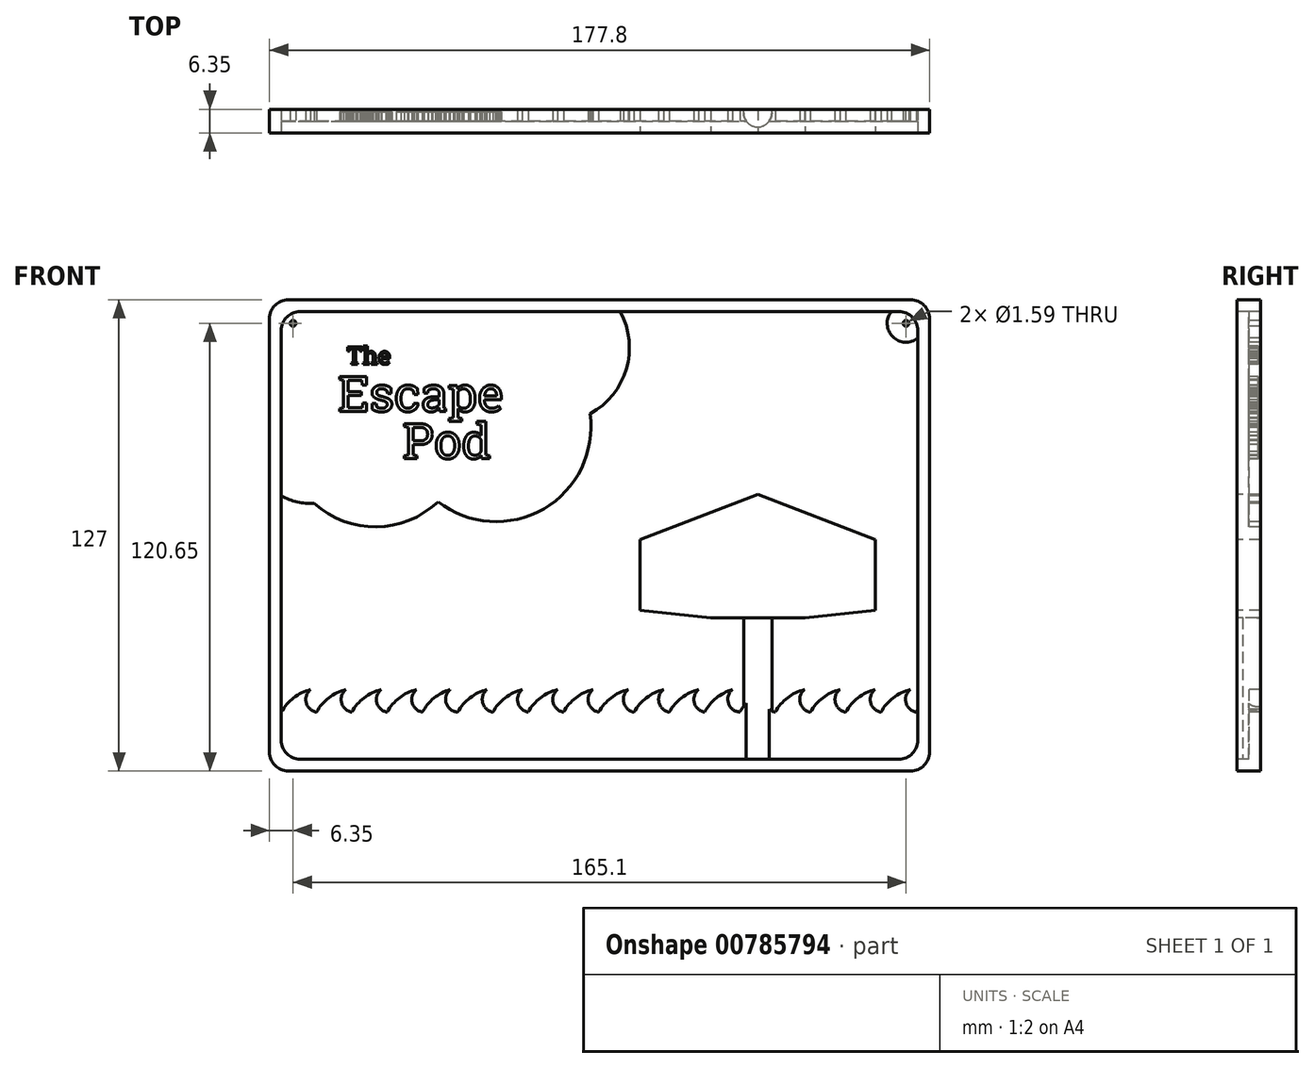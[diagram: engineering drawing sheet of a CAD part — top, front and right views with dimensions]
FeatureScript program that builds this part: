
annotation { "Feature Type Name" : "Feature", "Feature Type Description" : "" }
export const myFeature = defineFeature(function(context is Context, id is Id, definition is map)
    precondition{}
    {
        {
            var Q0;
            Q0=qCreatedBy(makeId("Front.planeOp"),FACE);
            var sketch = newSketch(context, id + "F0", { "sketchPlane" : qUnion([Q0])});
            skLineSegment(sketch, "E0.bottom", {"start": v(0, 0) * mm, "end": v(177.8, 0) * mm});
            skLineSegment(sketch, "E0.top", {"start": v(0, 127) * mm, "end": v(177.8, 127) * mm});
            skLineSegment(sketch, "E0.left", {"start": v(0, 0) * mm, "end": v(0, 127) * mm});
            skLineSegment(sketch, "E0.right", {"start": v(177.8, 0) * mm, "end": v(177.8, 127) * mm});
            skSolve(sketch);
        }
        {
            var Q0;
            Q0 = qSketchRegion(id + "F0", true);
            extrude(context, id + "F1", {"entities" : qUnion([Q0]), "depth" : 6.35 * mm, "offsetDistance" : 25.4 * mm});
        }
        {
            var Q0;
            Q0=makeQuery(id+"F1.opExtrude","CAP_FACE",FACE,{"disambiguationData":[OSD([sQuery(id+"F0.wireOp",EDGE,"E0.bottom"),sQuery(id+"F0.wireOp",EDGE,"E0.top"),sQuery(id+"F0.wireOp",EDGE,"E0.left"),sQuery(id+"F0.wireOp",EDGE,"E0.right")])],"isStart":false});
            var sketch = newSketch(context, id + "F2", { "sketchPlane" : qUnion([Q0])});
            skLineSegment(sketch, "E1.bottom", {"start": v(3.17, 123.83) * mm, "end": v(174.62, 123.83) * mm});
            skLineSegment(sketch, "E1.top", {"start": v(3.18, 3.17) * mm, "end": v(174.62, 3.17) * mm});
            skLineSegment(sketch, "E1.left", {"start": v(3.17, 123.83) * mm, "end": v(3.18, 3.17) * mm});
            skLineSegment(sketch, "E1.right", {"start": v(174.62, 123.83) * mm, "end": v(174.62, 3.18) * mm});
            skSolve(sketch);
        }
        {
            var Q0;
            Q0=makeQuery(id+"F2.imprint","IMPRINT",FACE,{"disambiguationData":[TD([[makeQuery(id+"F2.imprint","IMPRINT",EDGE,{"derivedFrom":sQuery(id+"F2.wireOp",EDGE,"E1.bottom")}),-1.0]])]});
            extrude(context, id + "F3", {"entities" : qUnion([Q0]), "operationType" : NewBodyOperationType.REMOVE, "oppositeDirection" : true, "depth" : 3.17 * mm, "offsetDistance" : 25.4 * mm});
        }
        {
            var Q0;
            Q0=makeQuery(id+"F1.opExtrude","SWEPT_EDGE",EDGE,{"disambiguationData":[OSD([sQuery(id+"F0.wireOp",EDGE,"E0.top"),sQuery(id+"F0.wireOp",EDGE,"E0.left")])]});
            var Q1;
            Q1=makeQuery(id+"F3.boolean.opBoolean","COPY",EDGE,{"derivedFrom":makeQuery(id+"F3.opExtrude","SWEPT_EDGE",EDGE,{"disambiguationData":[OSD([sQuery(id+"F2.wireOp",EDGE,"E1.bottom"),sQuery(id+"F2.wireOp",EDGE,"E1.left")])]})});
            var Q2;
            Q2=makeQuery(id+"F1.opExtrude","SWEPT_EDGE",EDGE,{"disambiguationData":[OSD([sQuery(id+"F0.wireOp",EDGE,"E0.top"),sQuery(id+"F0.wireOp",EDGE,"E0.right")])]});
            var Q3;
            Q3=makeQuery(id+"F3.boolean.opBoolean","COPY",EDGE,{"derivedFrom":makeQuery(id+"F3.opExtrude","SWEPT_EDGE",EDGE,{"disambiguationData":[OSD([sQuery(id+"F2.wireOp",EDGE,"E1.bottom"),sQuery(id+"F2.wireOp",EDGE,"E1.right")])]})});
            var Q4;
            Q4=makeQuery(id+"F1.opExtrude","SWEPT_EDGE",EDGE,{"disambiguationData":[OSD([sQuery(id+"F0.wireOp",EDGE,"E0.bottom"),sQuery(id+"F0.wireOp",EDGE,"E0.right")])]});
            var Q5;
            Q5=makeQuery(id+"F3.boolean.opBoolean","COPY",EDGE,{"derivedFrom":makeQuery(id+"F3.opExtrude","SWEPT_EDGE",EDGE,{"disambiguationData":[OSD([sQuery(id+"F2.wireOp",EDGE,"E1.top"),sQuery(id+"F2.wireOp",EDGE,"E1.right")])]})});
            var Q6;
            Q6=makeQuery(id+"F1.opExtrude","SWEPT_EDGE",EDGE,{"disambiguationData":[OSD([sQuery(id+"F0.wireOp",EDGE,"E0.bottom"),sQuery(id+"F0.wireOp",EDGE,"E0.left")])]});
            var Q7;
            Q7=makeQuery(id+"F3.boolean.opBoolean","COPY",EDGE,{"derivedFrom":makeQuery(id+"F3.opExtrude","SWEPT_EDGE",EDGE,{"disambiguationData":[OSD([sQuery(id+"F2.wireOp",EDGE,"E1.top"),sQuery(id+"F2.wireOp",EDGE,"E1.left")])]})});
            fillet(context, id + "F4", {"entities" : qUnion([Q0, Q1, Q2, Q3, Q4, Q5, Q6, Q7]), "radius" : 5.08 * mm, "tangentPropagation" : true, "allowEdgeOverflow" : false});
        }
        {
            var Q0;
            Q0=makeQuery(id+"F3.boolean.opBoolean","COPY",FACE,{"derivedFrom":makeQuery(id+"F3.opExtrude","CAP_FACE",FACE,{"disambiguationData":[OSD([sQuery(id+"F2.wireOp",EDGE,"E1.bottom"),sQuery(id+"F2.wireOp",EDGE,"E1.top"),sQuery(id+"F2.wireOp",EDGE,"E1.left"),sQuery(id+"F2.wireOp",EDGE,"E1.right")])],"isStart":false})});
            var sketch = newSketch(context, id + "F5", { "sketchPlane" : qUnion([Q0])});
            skArc(sketch, "E2", {"start": v(3.17, 74.14) * mm, "mid": v(7.49, 72.53) * mm, "end": v(12.07, 72.13) * mm});
            skLineSegment(sketch, "E3", {"start": v(47.44, 123.83) * mm, "end": v(148.94, 123.83) * mm});
            skLineSegment(sketch, "E4", {"start": v(3.17, 74.14) * mm, "end": v(3.17, 123.83) * mm});
            skLineSegment(sketch, "E5", {"start": v(47.44, 123.83) * mm, "end": v(3.17, 123.83) * mm});
            skArc(sketch, "E6", {"start": v(86.34, 96.26) * mm, "mid": v(96.1, 108.36) * mm, "end": v(94.49, 123.83) * mm});
            skArc(sketch, "E7", {"start": v(45.38, 72.57) * mm, "mid": v(73.83, 70.63) * mm, "end": v(86.34, 96.26) * mm});
            skArc(sketch, "E8", {"start": v(12.07, 72.13) * mm, "mid": v(28.81, 65.8) * mm, "end": v(45.38, 72.57) * mm});
            skSolve(sketch);
        }
        {
            var Q0;
            {var subQ0=sQuery(id+"F5.wireOp",EDGE,"E2");Q0=makeQuery(id+"F5.imprint","IMPRINT",FACE,{"disambiguationData":[TD([[makeQuery(id+"F5.imprint","IMPRINT",EDGE,{"derivedFrom":subQ0}),1.0]])]});}
            var sketch = newSketch(context, id + "F6", { "sketchPlane" : qUnion([Q0])});
            skText(sketch, "E9", { "text": "The", "fontName": "RobotoSlab-Regular.ttf"});
            skText(sketch, "E10", { "text": "Escape", "fontName": "RobotoSlab-Regular.ttf"});
            skText(sketch, "E11", { "text": "Pod", "fontName": "RobotoSlab-Regular.ttf"});
            const initialGuessF6  = {"E9": [0.02091, 0.1096, 1, 0, 0.0047], "E10": [0.01841, 0.0969, 1, 0, 0.00952], "E11": [0.03591, 0.0842, 1, 0, 0.00952]};
            skSetInitialGuess(sketch, initialGuessF6);
            skSolve(sketch);
        }
        {
            var Q0;
            Q0 = qSketchRegion(id + "F6", true);
            extrude(context, id + "F7", {"entities" : qUnion([Q0]), "operationType" : NewBodyOperationType.REMOVE, "oppositeDirection" : true, "depth" : 2.54 * mm, "offsetDistance" : 25.4 * mm});
        }
        {
            var Q0;
            {var subQ10=sQuery(id+"F5.wireOp",EDGE,"E2");Q0=makeQuery(id+"F5.imprint","IMPRINT",FACE,{"disambiguationData":[TD([[makeQuery(id+"F5.imprint","IMPRINT",EDGE,{"derivedFrom":subQ10}),-1.0]])]});}
            var sketch = newSketch(context, id + "F8", { "sketchPlane" : qUnion([Q0])});
            skSolve(sketch);
        }
        {
            var Q0;
            {var subQ10=sQuery(id+"F5.wireOp",EDGE,"E2");Q0=makeQuery(id+"F8.imprint","IMPRINT",FACE,{"disambiguationData":[TD([[makeQuery(id+"F8.imprint","IMPRINT",EDGE,{"derivedFrom":makeQuery(id+"F5.imprint","IMPRINT",EDGE,{"derivedFrom":subQ10})}),-1.0]])]});}
            var sketch = newSketch(context, id + "F9", { "sketchPlane" : qUnion([Q0])});
            skLineSegment(sketch, "E12.top", {"start": v(3.17, 3.17) * mm, "end": v(174.62, 3.17) * mm});
            skLineSegment(sketch, "E12.left", {"start": v(3.17, 28.58) * mm, "end": v(3.18, 3.17) * mm});
            skLineSegment(sketch, "E12.right", {"start": v(174.62, 66.14) * mm, "end": v(174.62, 3.17) * mm});
            skArc(sketch, "E13", {"start": v(11.09, 21.94) * mm, "mid": v(6.51, 19.72) * mm, "end": v(3.17, 15.88) * mm});
            skArc(sketch, "E14", {"start": v(11.09, 21.94) * mm, "mid": v(9.91, 18.4) * mm, "end": v(12.68, 15.88) * mm});
            skArc(sketch, "E15", {"start": v(20.59, 21.94) * mm, "mid": v(16.01, 19.72) * mm, "end": v(12.68, 15.88) * mm});
            skArc(sketch, "E16", {"start": v(20.59, 21.94) * mm, "mid": v(19.41, 18.4) * mm, "end": v(22.18, 15.88) * mm});
            skArc(sketch, "E17", {"start": v(30.09, 21.94) * mm, "mid": v(25.51, 19.72) * mm, "end": v(22.18, 15.88) * mm});
            skArc(sketch, "E18", {"start": v(30.09, 21.94) * mm, "mid": v(28.91, 18.4) * mm, "end": v(31.68, 15.88) * mm});
            skArc(sketch, "E19", {"start": v(39.59, 21.94) * mm, "mid": v(35.01, 19.72) * mm, "end": v(31.68, 15.88) * mm});
            skArc(sketch, "E20", {"start": v(39.59, 21.94) * mm, "mid": v(38.41, 18.4) * mm, "end": v(41.18, 15.88) * mm});
            skArc(sketch, "E21", {"start": v(48.67, 21.94) * mm, "mid": v(44.33, 19.65) * mm, "end": v(41.18, 15.88) * mm});
            skArc(sketch, "E22", {"start": v(48.67, 21.94) * mm, "mid": v(47.6, 18.22) * mm, "end": v(50.68, 15.88) * mm});
            skArc(sketch, "E23", {"start": v(58.59, 21.94) * mm, "mid": v(54.01, 19.72) * mm, "end": v(50.68, 15.88) * mm});
            skArc(sketch, "E24", {"start": v(58.59, 21.94) * mm, "mid": v(57.41, 18.4) * mm, "end": v(60.18, 15.88) * mm});
            skArc(sketch, "E25", {"start": v(68.09, 21.94) * mm, "mid": v(63.51, 19.72) * mm, "end": v(60.18, 15.88) * mm});
            skArc(sketch, "E26", {"start": v(68.09, 21.94) * mm, "mid": v(66.92, 18.4) * mm, "end": v(69.68, 15.88) * mm});
            skArc(sketch, "E27", {"start": v(77.6, 21.94) * mm, "mid": v(73.02, 19.72) * mm, "end": v(69.68, 15.88) * mm});
            skArc(sketch, "E28", {"start": v(77.6, 21.94) * mm, "mid": v(76.42, 18.4) * mm, "end": v(79.18, 15.88) * mm});
            skArc(sketch, "E29", {"start": v(87.1, 21.94) * mm, "mid": v(82.52, 19.72) * mm, "end": v(79.18, 15.88) * mm});
            skArc(sketch, "E30", {"start": v(87.1, 21.94) * mm, "mid": v(85.92, 18.4) * mm, "end": v(88.68, 15.88) * mm});
            skArc(sketch, "E31", {"start": v(96.6, 21.94) * mm, "mid": v(92.02, 19.72) * mm, "end": v(88.68, 15.88) * mm});
            skArc(sketch, "E32", {"start": v(96.6, 21.94) * mm, "mid": v(95.42, 18.4) * mm, "end": v(98.18, 15.88) * mm});
            skArc(sketch, "E33", {"start": v(106.1, 21.94) * mm, "mid": v(101.52, 19.72) * mm, "end": v(98.18, 15.88) * mm});
            skArc(sketch, "E34", {"start": v(106.1, 21.94) * mm, "mid": v(104.92, 18.4) * mm, "end": v(107.68, 15.87) * mm});
            skArc(sketch, "E35", {"start": v(115.6, 21.94) * mm, "mid": v(111.02, 19.72) * mm, "end": v(107.68, 15.88) * mm});
            skArc(sketch, "E36", {"start": v(115.6, 21.94) * mm, "mid": v(114.42, 18.4) * mm, "end": v(117.19, 15.88) * mm});
            skArc(sketch, "E37", {"start": v(124.68, 21.94) * mm, "mid": v(120.33, 19.65) * mm, "end": v(117.19, 15.88) * mm});
            skArc(sketch, "E38", {"start": v(124.68, 21.94) * mm, "mid": v(123.61, 18.22) * mm, "end": v(126.68, 15.88) * mm});
            skArc(sketch, "E39", {"start": v(134.6, 21.94) * mm, "mid": v(130.02, 19.72) * mm, "end": v(126.68, 15.88) * mm});
            skArc(sketch, "E40", {"start": v(134.6, 21.94) * mm, "mid": v(133.42, 18.4) * mm, "end": v(136.19, 15.88) * mm});
            skArc(sketch, "E41", {"start": v(144.1, 21.94) * mm, "mid": v(139.52, 19.72) * mm, "end": v(136.19, 15.88) * mm});
            skArc(sketch, "E42", {"start": v(144.1, 21.94) * mm, "mid": v(142.92, 18.4) * mm, "end": v(145.69, 15.88) * mm});
            skArc(sketch, "E43", {"start": v(153.6, 21.94) * mm, "mid": v(149.02, 19.72) * mm, "end": v(145.69, 15.87) * mm});
            skArc(sketch, "E44", {"start": v(153.6, 21.94) * mm, "mid": v(152.42, 18.4) * mm, "end": v(155.19, 15.88) * mm});
            skArc(sketch, "E45", {"start": v(163.1, 21.94) * mm, "mid": v(158.52, 19.72) * mm, "end": v(155.19, 15.88) * mm});
            skArc(sketch, "E46", {"start": v(163.1, 21.94) * mm, "mid": v(161.92, 18.4) * mm, "end": v(164.69, 15.88) * mm});
            skArc(sketch, "E47", {"start": v(172.6, 21.94) * mm, "mid": v(168.02, 19.72) * mm, "end": v(164.69, 15.88) * mm});
            skArc(sketch, "E48", {"start": v(172.6, 21.94) * mm, "mid": v(171.42, 18.4) * mm, "end": v(174.19, 15.88) * mm});
            skArc(sketch, "E49", {"start": v(174.62, 16.6) * mm, "mid": v(174.4, 16.24) * mm, "end": v(174.19, 15.88) * mm});
            skPoint(sketch, "E50.end.orphan", {"position": v(183.7, 15.88) * mm});
            skSolve(sketch);
        }
        {
            var Q0;
            {var subQ18=sQuery(id+"F9.wireOp",EDGE,"E13");Q0=makeQuery(id+"F9.imprint","IMPRINT",FACE,{"disambiguationData":[TD([[makeQuery(id+"F9.imprint","IMPRINT",EDGE,{"derivedFrom":subQ18}),-1.0]])]});}
            extrude(context, id + "F10", {"entities" : qUnion([Q0]), "operationType" : NewBodyOperationType.REMOVE, "oppositeDirection" : true, "depth" : 25.4 * mm, "offsetDistance" : 25.4 * mm});
        }
        {
            var Q0;
            {var subQ10=sQuery(id+"F5.wireOp",EDGE,"E2");Q0=makeQuery(id+"F5.imprint","IMPRINT",FACE,{"disambiguationData":[TD([[makeQuery(id+"F5.imprint","IMPRINT",EDGE,{"derivedFrom":subQ10}),-1.0]])]});}
            var sketch = newSketch(context, id + "F11", { "sketchPlane" : qUnion([Q0])});
            skLineSegment(sketch, "E51.bottom", {"start": v(127.69, 41.27) * mm, "end": v(135.3, 41.27) * mm});
            skLineSegment(sketch, "E51.top", {"start": v(127.69, 3.17) * mm, "end": v(135.3, 3.17) * mm});
            skLineSegment(sketch, "E51.left", {"start": v(127.69, 41.27) * mm, "end": v(127.69, 3.17) * mm});
            skLineSegment(sketch, "E51.right", {"start": v(135.3, 41.27) * mm, "end": v(135.3, 3.17) * mm});
            skSolve(sketch);
        }
        {
            var Q0;
            Q0=makeQuery(id+"F11.imprint","IMPRINT",FACE,{"disambiguationData":[TD([[makeQuery(id+"F11.imprint","IMPRINT",EDGE,{"derivedFrom":sQuery(id+"F11.wireOp",EDGE,"E51.bottom")}),-1.0]])]});
            extrude(context, id + "F12", {"entities" : qUnion([Q0]), "operationType" : NewBodyOperationType.ADD, "depth" : 1.59 * mm, "offsetDistance" : 25.4 * mm});
        }
        {
            var Q0;
            {var subQ0=sQuery(id+"F0.wireOp",EDGE,"E0.right");var subQ1=sQuery(id+"F0.wireOp",EDGE,"E0.top");var subQ2=sQuery(id+"F0.wireOp",EDGE,"E0.left");var subQ3=sQuery(id+"F0.wireOp",EDGE,"E0.bottom");Q0=makeQuery(id+"F7.boolean.opBoolean","SPLIT",FACE,{"disambiguationData":[TD([makeQuery(id+"F1.opExtrude","SWEPT_FACE",FACE,{"disambiguationData":[OSD([subQ3])]})])],"derivedFrom":makeQuery(id+"F1.opExtrude","CAP_FACE",FACE,{"disambiguationData":[OSD([subQ3,subQ1,subQ2,subQ0])],"isStart":true})});}
            var sketch = newSketch(context, id + "F13", { "sketchPlane" : qUnion([Q0])});
            skLineSegment(sketch, "E52.bottom", {"start": v(-135.3, 41.27) * mm, "end": v(-127.69, 41.27) * mm});
            skLineSegment(sketch, "E52.top", {"start": v(-135.3, 3.17) * mm, "end": v(-127.69, 3.17) * mm});
            skLineSegment(sketch, "E52.left", {"start": v(-135.3, 41.27) * mm, "end": v(-135.3, 3.17) * mm});
            skLineSegment(sketch, "E52.right", {"start": v(-127.69, 41.27) * mm, "end": v(-127.69, 3.17) * mm});
            skSolve(sketch);
        }
        {
            var Q0;
            {var subQ1=sQuery(id+"F13.wireOp",EDGE,"E52.bottom");Q0=makeQuery(id+"F13.imprint","IMPRINT",FACE,{"disambiguationData":[TD([[makeQuery(id+"F13.imprint","IMPRINT",EDGE,{"derivedFrom":subQ1}),-1.0]])]});}
            extrude(context, id + "F14", {"entities" : qUnion([Q0]), "operationType" : NewBodyOperationType.ADD, "oppositeDirection" : true, "depth" : 3.17 * mm, "offsetDistance" : 25.4 * mm});
        }
        {
            var Q0;
            {var subQ0=sQuery(id+"F0.wireOp",EDGE,"E0.right");var subQ1=sQuery(id+"F0.wireOp",EDGE,"E0.top");var subQ2=sQuery(id+"F0.wireOp",EDGE,"E0.left");var subQ3=sQuery(id+"F0.wireOp",EDGE,"E0.bottom");var subQ4=makeQuery(id+"F7.boolean.opBoolean","SPLIT",FACE,{"disambiguationData":[TD([makeQuery(id+"F1.opExtrude","SWEPT_FACE",FACE,{"disambiguationData":[OSD([subQ3])]})])],"derivedFrom":makeQuery(id+"F1.opExtrude","CAP_FACE",FACE,{"disambiguationData":[OSD([subQ3,subQ1,subQ2,subQ0])],"isStart":true})});var subQ5=makeQuery(id+"FdCLAQgDWUUzLun_1.boolean.opBoolean","INTERSECT",EDGE,{"derivedFrom":[subQ4,makeQuery(id+"FdCLAQgDWUUzLun_1.opExtrude","SWEPT_FACE",FACE,{"disambiguationData":[OSD([sQuery(id+"F5PyO3ddK9HHKjI_1.wireOp",EDGE,"8fb3529d-b777-476a-a323-f7732f18a75f")])]})]});var subQ8=sQuery(id+"F13.wireOp",EDGE,"E52.left");var subQ9=makeQuery(id+"F13.imprint","INTERSECT",VERTEX,{"derivedFrom":[subQ5,subQ8]});Q0=makeQuery(id+"F13.imprint","IMPRINT",FACE,{"disambiguationData":[TD([[makeQuery(id+"F13.imprint","IMPRINT",EDGE,{"disambiguationData":[TD([[subQ9,-1.0]])],"derivedFrom":subQ8}),1.0]])]});}
            extrude(context, id + "F15", {"entities" : qUnion([Q0]), "operationType" : NewBodyOperationType.ADD, "oppositeDirection" : true, "depth" : 3.17 * mm, "offsetDistance" : 25.4 * mm});
        }
        {
            var Q0;
            Q0=makeQuery(id+"F12.opExtrude","CAP_EDGE",EDGE,{"disambiguationData":[OSD([sQuery(id+"F11.wireOp",EDGE,"E51.right")])],"isStart":false});
            var Q1;
            Q1=makeQuery(id+"F12.opExtrude","CAP_EDGE",EDGE,{"disambiguationData":[OSD([sQuery(id+"F11.wireOp",EDGE,"E51.left")])],"isStart":false});
            fillet(context, id + "F16", {"entities" : qUnion([Q0, Q1]), "radius" : 3.8 * mm, "tangentPropagation" : true, "allowEdgeOverflow" : false});
        }
        {
            var Q0;
            {var subQ10=sQuery(id+"F5.wireOp",EDGE,"E2");Q0=makeQuery(id+"F5.imprint","IMPRINT",FACE,{"disambiguationData":[TD([[makeQuery(id+"F5.imprint","IMPRINT",EDGE,{"derivedFrom":subQ10}),-1.0]])]});}
            var sketch = newSketch(context, id + "F17", { "sketchPlane" : qUnion([Q0])});
            skLineSegment(sketch, "E53.bottom", {"start": v(144.2, 60.32) * mm, "end": v(118.8, 60.32) * mm});
            skLineSegment(sketch, "E53.top", {"start": v(144.2, 41.27) * mm, "end": v(118.8, 41.27) * mm});
            skLineSegment(sketch, "E53.left", {"start": v(144.2, 60.32) * mm, "end": v(144.2, 41.27) * mm});
            skLineSegment(sketch, "E53.right", {"start": v(118.8, 60.32) * mm, "end": v(118.8, 41.27) * mm});
            skLineSegment(sketch, "E54", {"start": v(118.8, 41.27) * mm, "end": v(99.85, 43.27) * mm});
            skLineSegment(sketch, "E55", {"start": v(118.8, 60.32) * mm, "end": v(99.85, 62.32) * mm});
            skLineSegment(sketch, "E56", {"start": v(99.85, 62.32) * mm, "end": v(99.85, 43.27) * mm});
            skLineSegment(sketch, "E57", {"start": v(144.2, 41.27) * mm, "end": v(163.14, 43.27) * mm});
            skLineSegment(sketch, "E58", {"start": v(163.14, 43.27) * mm, "end": v(163.14, 62.32) * mm});
            skLineSegment(sketch, "E59", {"start": v(163.14, 62.32) * mm, "end": v(144.2, 60.32) * mm});
            skLineSegment(sketch, "E60", {"start": v(118.8, 60.32) * mm, "end": v(131.5, 74.52) * mm});
            skLineSegment(sketch, "E61", {"start": v(144.2, 60.32) * mm, "end": v(131.5, 74.52) * mm});
            skLineSegment(sketch, "E62", {"start": v(99.85, 62.32) * mm, "end": v(131.5, 74.52) * mm});
            skLineSegment(sketch, "E63", {"start": v(131.5, 74.52) * mm, "end": v(163.14, 62.32) * mm});
            skSolve(sketch);
        }
        {
            var Q0;
            Q0=makeQuery(id+"F17.imprint","IMPRINT",FACE,{"disambiguationData":[TD([[makeQuery(id+"F17.imprint","IMPRINT",EDGE,{"derivedFrom":sQuery(id+"F17.wireOp",EDGE,"E53.bottom")}),1.0]])]});
            var Q1;
            Q1=makeQuery(id+"F17.imprint","IMPRINT",FACE,{"disambiguationData":[TD([[makeQuery(id+"F17.imprint","IMPRINT",EDGE,{"derivedFrom":sQuery(id+"F17.wireOp",EDGE,"E55")}),-1.0]])]});
            var Q2;
            Q2=makeQuery(id+"F17.imprint","IMPRINT",FACE,{"disambiguationData":[TD([[makeQuery(id+"F17.imprint","IMPRINT",EDGE,{"derivedFrom":sQuery(id+"F17.wireOp",EDGE,"E53.right")}),-1.0]])]});
            var Q3;
            Q3=makeQuery(id+"F17.imprint","IMPRINT",FACE,{"disambiguationData":[TD([[makeQuery(id+"F17.imprint","IMPRINT",EDGE,{"derivedFrom":sQuery(id+"F17.wireOp",EDGE,"E53.bottom")}),-1.0]])]});
            var Q4;
            Q4=makeQuery(id+"F17.imprint","IMPRINT",FACE,{"disambiguationData":[TD([[makeQuery(id+"F17.imprint","IMPRINT",EDGE,{"derivedFrom":sQuery(id+"F17.wireOp",EDGE,"E59")}),-1.0]])]});
            var Q5;
            Q5=makeQuery(id+"F17.imprint","IMPRINT",FACE,{"disambiguationData":[TD([[makeQuery(id+"F17.imprint","IMPRINT",EDGE,{"derivedFrom":sQuery(id+"F17.wireOp",EDGE,"E53.left")}),1.0]])]});
            extrude(context, id + "F18", {"entities" : qUnion([Q0, Q1, Q2, Q3, Q4, Q5]), "operationType" : NewBodyOperationType.ADD, "oppositeDirection" : true, "depth" : 3.17 * mm, "offsetDistance" : 25.4 * mm});
        }
        {
            var Q0;
            Q0=makeQuery(id+"F17.imprint","IMPRINT",FACE,{"disambiguationData":[TD([[makeQuery(id+"F17.imprint","IMPRINT",EDGE,{"derivedFrom":sQuery(id+"F17.wireOp",EDGE,"E53.bottom")}),1.0]])]});
            var Q1;
            Q1=makeQuery(id+"F17.imprint","IMPRINT",FACE,{"disambiguationData":[TD([[makeQuery(id+"F17.imprint","IMPRINT",EDGE,{"derivedFrom":sQuery(id+"F17.wireOp",EDGE,"E53.left")}),1.0]])]});
            var Q2;
            Q2=makeQuery(id+"F17.imprint","IMPRINT",FACE,{"disambiguationData":[TD([[makeQuery(id+"F17.imprint","IMPRINT",EDGE,{"derivedFrom":sQuery(id+"F17.wireOp",EDGE,"E53.right")}),-1.0]])]});
            extrude(context, id + "F19", {"entities" : qUnion([Q0, Q1, Q2]), "operationType" : NewBodyOperationType.ADD, "depth" : 3.17 * mm, "offsetDistance" : 25.4 * mm});
        }
        {
            var Q0;
            Q0=sQuery(id+"F17.wireOp",EDGE,"E53.right");
            extrude(context, id + "F20", {"bodyType" : ToolBodyType.SURFACE, "surfaceEntities" : qUnion([Q0]), "depth" : 3.3 * mm, "offsetDistance" : 25.4 * mm});
        }
        {
            var Q0;
            Q0=sQuery(id+"F17.wireOp",EDGE,"E60");
            var Q1;
            Q1=sQuery(id+"F17.wireOp",EDGE,"E61");
            var Q2;
            Q2=sQuery(id+"F17.wireOp",EDGE,"E53.left");
            extrude(context, id + "F21", {"bodyType" : ToolBodyType.SURFACE, "surfaceEntities" : qUnion([Q0, Q1, Q2]), "depth" : 3.3 * mm, "offsetDistance" : 25.4 * mm});
        }
        {
            var Q0;
            Q0=makeQuery(id+"F17.imprint","IMPRINT",FACE,{"disambiguationData":[TD([[makeQuery(id+"F17.imprint","IMPRINT",EDGE,{"derivedFrom":sQuery(id+"F17.wireOp",EDGE,"E55")}),-1.0]])]});
            var Q1;
            Q1=makeQuery(id+"F17.imprint","IMPRINT",FACE,{"disambiguationData":[TD([[makeQuery(id+"F17.imprint","IMPRINT",EDGE,{"derivedFrom":sQuery(id+"F17.wireOp",EDGE,"E53.bottom")}),-1.0]])]});
            var Q2;
            Q2=makeQuery(id+"F17.imprint","IMPRINT",FACE,{"disambiguationData":[TD([[makeQuery(id+"F17.imprint","IMPRINT",EDGE,{"derivedFrom":sQuery(id+"F17.wireOp",EDGE,"E59")}),-1.0]])]});
            extrude(context, id + "F22", {"entities" : qUnion([Q0, Q1, Q2]), "operationType" : NewBodyOperationType.ADD, "depth" : 3.17 * mm, "offsetDistance" : 25.4 * mm});
        }
        {
            var Q0;
            Q0=sQuery(id+"F17.wireOp",EDGE,"E55");
            var Q1;
            Q1=sQuery(id+"F17.wireOp",EDGE,"E53.bottom");
            var Q2;
            Q2=sQuery(id+"F17.wireOp",EDGE,"E59");
            extrude(context, id + "F23", {"bodyType" : ToolBodyType.SURFACE, "surfaceEntities" : qUnion([Q0, Q1, Q2]), "depth" : 3.17 * mm, "offsetDistance" : 25.4 * mm});
        }
        {
            var Q0;
            {var subQ4=sQuery(id+"F5.wireOp",EDGE,"E2");Q0=makeQuery(id+"F5.imprint","IMPRINT",FACE,{"disambiguationData":[TD([[makeQuery(id+"F5.imprint","IMPRINT",EDGE,{"derivedFrom":subQ4}),1.0]])]});}
            var sketch = newSketch(context, id + "F24", { "sketchPlane" : qUnion([Q0])});
            skCircle(sketch, "E64", {"center": v(6.35, 120.65) * mm, "radius": 0.8 * mm});
            skCircle(sketch, "E65", {"center": v(171.45, 120.65) * mm, "radius": 5.08 * mm});
            skCircle(sketch, "E66", {"center": v(171.45, 120.65) * mm, "radius": 0.8 * mm});
            skSolve(sketch);
        }
        {
            var Q0;
            Q0=makeQuery(id+"F24.imprint","IMPRINT",FACE,{"disambiguationData":[TD([[makeQuery(id+"F24.imprint","IMPRINT",EDGE,{"derivedFrom":sQuery(id+"F24.wireOp",EDGE,"E65")}),1.0]])]});
            var Q1;
            Q1=sQuery(id+"F24.wireOp",EDGE,"E65");
            extrude(context, id + "F25", {"entities" : qUnion([Q0]), "operationType" : NewBodyOperationType.ADD, "surfaceEntities" : qUnion([Q1]), "oppositeDirection" : true, "depth" : 3.17 * mm, "offsetDistance" : 25.4 * mm});
        }
        {
            var Q0;
            Q0=makeQuery(id+"F24.imprint","IMPRINT",FACE,{"disambiguationData":[TD([[makeQuery(id+"F24.imprint","IMPRINT",EDGE,{"derivedFrom":sQuery(id+"F24.wireOp",EDGE,"E64")}),1.0]])]});
            extrude(context, id + "F26", {"entities" : qUnion([Q0]), "operationType" : NewBodyOperationType.REMOVE, "oppositeDirection" : true, "depth" : 25.4 * mm, "offsetDistance" : 25.4 * mm});
        }
    });
